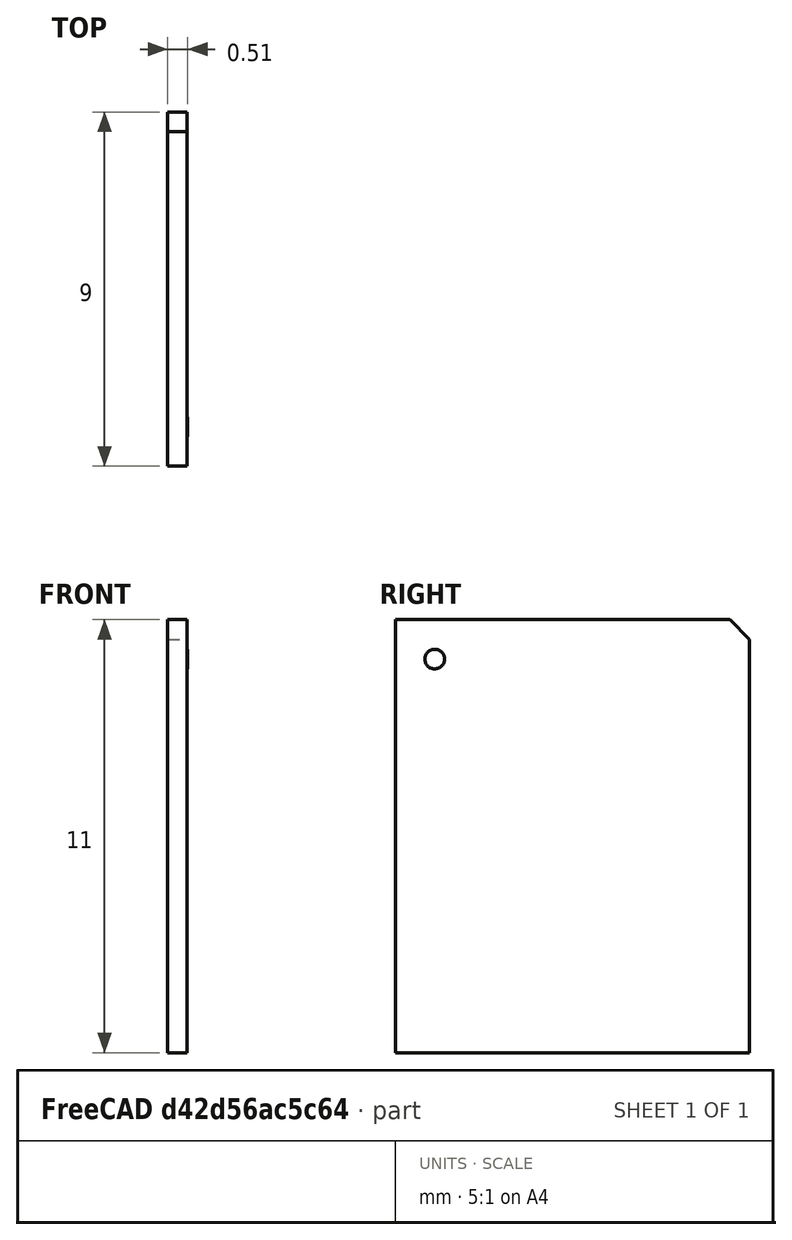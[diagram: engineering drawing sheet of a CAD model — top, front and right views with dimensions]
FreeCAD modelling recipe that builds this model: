
FCSTD DOCUMENT  (FreeCAD 1.1R20260108 (Git shallow))
Label: LiNbO3_Substrate_10mm
License: All rights reserved
LicenseURL: https://en.wikipedia.org/wiki/All_rights_reserved
objects: TechDraw::DrawViewAnnotation×5, TechDraw::DrawViewDimension×4, Sketcher::SketchObject×2, PartDesign::Pad×2, TechDraw::DrawProjGroupItem×2, App::Point×1, TechDraw::DrawSVGTemplate×1, PartDesign::Body×1, TechDraw::DrawProjGroup×1, TechDraw::DrawPage×1
note: 19 computed .brp shape members not serialized (recipe doc carries the construction recipe); baked Part::Feature solids carry a one-line shape summary decoded from their .brp

FEATURE [App::Point] Origin001
  Role = Origin
FEATURE [Sketcher::SketchObject] Sketch
  ArcFitTolerance = 1e-06
  AttachmentSupport = -> [Origin]
  ExternalTypes = [0]
  FullyConstrained = true
  MakeInternals = false
  MapMode = 5
  Placement = pos=(0,0,0) rot=(0.57735,0.57735,0.57735;2.0944rad)
  sketch-geometry (9):
    g0: LineSegment [constr] StartX=-4.5 StartY=-5.5 StartZ=0 EndX=4.5 EndY=-5.5 EndZ=0
    g1: LineSegment [constr] StartX=4.5 StartY=-5.5 StartZ=0 EndX=4.5 EndY=5.5 EndZ=0
    g2: LineSegment [constr] StartX=4.5 StartY=5.5 StartZ=0 EndX=-4.5 EndY=5.5 EndZ=0
    g3: LineSegment [constr] StartX=-4.5 StartY=5.5 StartZ=0 EndX=-4.5 EndY=-5.5 EndZ=0
    g4: LineSegment StartX=-4.5 StartY=-5.5 StartZ=0 EndX=4.5 EndY=-5.5 EndZ=0
    g5: LineSegment StartX=4.5 StartY=-5.5 StartZ=0 EndX=4.5 EndY=5 EndZ=0
    g6: LineSegment StartX=4 StartY=5.5 StartZ=0 EndX=4.5 EndY=5 EndZ=0
    g7: LineSegment StartX=4 StartY=5.5 StartZ=0 EndX=-4.5 EndY=5.5 EndZ=0
    g8: LineSegment StartX=-4.5 StartY=5.5 StartZ=0 EndX=-4.5 EndY=-5.5 EndZ=0
  constraints (24):
    c: Coincident(g0,g1)
    c: Coincident(g1,g2)
    c: Coincident(g2,g3)
    c: Coincident(g3,g0)
    c: Horizontal(g0)
    c: Horizontal(g2)
    c: Vertical(g1)
    c: Vertical(g3)
    c: Distance(g2,g2) = 9
    c: DistanceX(g-2,g2) = -4.5
    c: DistanceY(g-1,g0) = -5.5
    c: Coincident(g4,g0)
    c: Coincident(g4,g0)
    c: Coincident(g5,g0)
    c: PointOnObject(g5,g1)
    c: PointOnObject(g6,g2)
    c: Coincident(g6,g5)
    c: Distance(g5,g1) = 0.5
    c: Distance(g1,g6) = 0.5
    c: Coincident(g7,g6)
    c: Coincident(g7,g2)
    c: Coincident(g8,g2)
    c: Coincident(g8,g0)
    c: DistanceY(g8,g8) = 11
FEATURE [PartDesign::Pad] Pad
  Direction = (1,0,0)
  Length = 0.5
  Length2 = 10
  Profile = -> Sketch
  ReferenceAxis = -> Sketch [N_Axis]
  Refine = true
  SideType = 0
  Suppressed = false
  Type = 0
  Type2 = 0
FEATURE [TechDraw::DrawSVGTemplate] Template
  Height = 210
  Orientation = 1
  Template = /Applications/FreeCAD.app/Contents/Resources/share/Mod/TechDraw/Templates/ISO/A4_Landscape_TD.svg
  Width = 297
FEATURE [Sketcher::SketchObject] Sketch001
  ArcFitTolerance = 1e-06
  AttachmentSupport = -> [Pad]
  ExternalGeometry = -> [Pad]
  ExternalTypes = [0,0]
  FullyConstrained = true
  MakeInternals = false
  MapMode = 5
  Placement = pos=(0.5,0,0) rot=(0.57735,0.57735,0.57735;2.0944rad)
  sketch-geometry (1):
    g0: Circle CenterX=-3.5 CenterY=4.5 CenterZ=0 NormalX=0 NormalY=0 NormalZ=1 AngleXU=0 Radius=0.25
  constraints (3):
    c: DistanceY(g0,g-4) = 1
    c: DistanceX(g-4,g0) = 1
    c: Diameter(g0) = 0.5
FEATURE [PartDesign::Pad] Pad001
  BaseFeature = -> Pad
  Direction = (1,0,0)
  Length = 0.01
  Length2 = 10
  Profile = -> Sketch001
  ReferenceAxis = -> Sketch001 [N_Axis]
  Refine = true
  SideType = 0
  Suppressed = false
  Type = 0
  Type2 = 0
FEATURE [PartDesign::Body] Body
  AllowCompound = false
  Group = -> [Sketch,Pad,Sketch001,Pad001]
  Origin = -> Origin
  Tip = -> Pad001
FEATURE [TechDraw::DrawProjGroupItem] ProjItem  label="Front"
  CoarseView = false
  Direction = (1,0,0)
  Focus = 100
  HardHidden = true
  IsoCount = 0
  IsoHidden = false
  IsoVisible = false
  LockPosition = true
  Perspective = false
  Rotation = 0
  RotationVector = (0,1,0)
  Scale = 5
  ScaleType = 2
  ScrubCount = 1
  SeamHidden = false
  SeamVisible = false
  SmoothHidden = false
  SmoothVisible = true
  Source = -> [Body]
  Type = 0
  X = 0
  XDirection = (0,1,0)
  Y = 0
FEATURE [TechDraw::DrawProjGroupItem] ProjItem001  label="FrontTopRight"
  CoarseView = false
  Direction = (0.57735,0.57735,0.57735)
  Focus = 100
  HardHidden = true
  IsoCount = 0
  IsoHidden = false
  IsoVisible = false
  LockPosition = false
  Perspective = false
  Rotation = 0
  RotationVector = (1,0,0)
  Scale = 5
  ScaleType = 2
  ScrubCount = 1
  SeamHidden = false
  SeamVisible = false
  SmoothHidden = false
  SmoothVisible = true
  Source = -> [Body]
  Type = 7
  X = -54.2938
  XDirection = (-0.707107,0.707107,0)
  Y = -74.6496
FEATURE [TechDraw::DrawProjGroup] ProjGroup
  Anchor = -> ProjItem
  AutoDistribute = true
  LockPosition = false
  ProjectionType = 0
  Rotation = 0
  Scale = 5
  ScaleType = 2
  Source = -> [Body]
  Views = -> [ProjItem,ProjItem001]
  X = 147.964
  Y = 136.218
  spacingX = 15
  spacingY = 15
FEATURE [TechDraw::DrawViewAnnotation] Annotation
  Font = osifont
  LineSpace = 100
  LockPosition = false
  MaxWidth = -1
  Rotation = 0
  ScaleType = 0
  Text = +Z
  TextSize = 5
  TextStyle = 0
  X = 93.6698
  Y = 110.213
FEATURE [TechDraw::DrawViewAnnotation] Annotation001
  Font = osifont
  LineSpace = 100
  LockPosition = false
  MaxWidth = -1
  Rotation = 0
  ScaleType = 0
  Text = +Y
  TextSize = 5
  TextStyle = 0
  X = 128.644
  Y = 42.1354
FEATURE [TechDraw::DrawViewAnnotation] Annotation002
  Font = osifont
  LineSpace = 100
  LockPosition = false
  MaxWidth = -1
  Rotation = 0
  ScaleType = 0
  Text = +X
  TextSize = 5
  TextStyle = 0
  X = 50.7535
  Y = 43.6687
FEATURE [TechDraw::DrawViewDimension] Dimension
  AngleOverride = false
  Arbitrary = false
  ArbitraryTolerances = false
  BoxCorners = (2) [(-22.5,-27.5,0),(22.5,27.5,0)]
  EqualTolerance = true
  ExtensionAngle = 0
  FormatSpec = %.2w
  FormatSpecOverTolerance = %+.2w
  FormatSpecUnderTolerance = %+.2w
  Inverted = false
  LineAngle = 0
  LockPosition = false
  MeasureType = 1
  OverTolerance = 0.2
  References2D = -> [ProjItem]
  Rotation = 0
  ScaleType = 0
  ShowUnits = false
  TheoreticalExact = false
  Type = 1
  UnderTolerance = -0.2
  UseActualArea = true
  X = 0
  Y = -32.9551
FEATURE [TechDraw::DrawViewDimension] Dimension001
  AngleOverride = false
  Arbitrary = false
  ArbitraryTolerances = false
  BoxCorners = (2) [(-22.5,-27.5,0),(22.5,27.5,0)]
  EqualTolerance = true
  ExtensionAngle = 0
  FormatSpec = %.2w
  FormatSpecOverTolerance = %+.2w
  FormatSpecUnderTolerance = %+.2w
  Inverted = false
  LineAngle = 0
  LockPosition = false
  MeasureType = 1
  OverTolerance = 0.2
  References2D = -> [ProjItem]
  Rotation = 0
  ScaleType = 0
  ShowUnits = false
  TheoreticalExact = false
  Type = 2
  UnderTolerance = -0.2
  UseActualArea = true
  X = -34.1514
  Y = 0
FEATURE [TechDraw::DrawViewDimension] Dimension002
  AngleOverride = false
  Arbitrary = true
  ArbitraryTolerances = false
  BoxCorners = (2) [(-22.5,-27.5,0),(22.5,27.5,0)]
  EqualTolerance = true
  ExtensionAngle = 0
  FormatSpec = approx. 1.0
  FormatSpecOverTolerance = %+.2w
  FormatSpecUnderTolerance = %+.2w
  Inverted = false
  LineAngle = 0
  LockPosition = false
  MeasureType = 1
  OverTolerance = 0
  References2D = -> [ProjItem]
  Rotation = 0
  ScaleType = 0
  ShowUnits = false
  TheoreticalExact = false
  Type = 1
  UnderTolerance = 0
  UseActualArea = true
  X = -42.4072
  Y = 38.9928
FEATURE [TechDraw::DrawViewDimension] Dimension003
  AngleOverride = false
  Arbitrary = true
  ArbitraryTolerances = false
  BoxCorners = (2) [(-22.5,-27.5,0),(22.5,27.5,0)]
  EqualTolerance = true
  ExtensionAngle = 0
  FormatSpec = approx. 0.5
  FormatSpecOverTolerance = %+.2w
  FormatSpecUnderTolerance = %+.2w
  Inverted = false
  LineAngle = 0
  LockPosition = false
  MeasureType = 1
  OverTolerance = 0
  References2D = -> [ProjItem]
  Rotation = 0
  ScaleType = 0
  ShowUnits = false
  TheoreticalExact = false
  Type = 1
  UnderTolerance = 0
  UseActualArea = true
  X = 43.4555
  Y = 38.9928
FEATURE [TechDraw::DrawViewAnnotation] Annotation003
  Font = osifont
  LineSpace = 100
  LockPosition = false
  MaxWidth = -1
  Rotation = 0
  ScaleType = 0
  Text = dye mark on +X face
  TextSize = 5
  TextStyle = 0
  X = 89.3922
  Y = 187.184
FEATURE [TechDraw::DrawViewAnnotation] Annotation004
  Font = osifont
  LineSpace = 100
  LockPosition = false
  MaxWidth = -1
  Rotation = 0
  ScaleType = 0
  Text = visible chamfer
  TextSize = 5
  TextStyle = 0
  X = 197.335
  Y = 187.184
FEATURE [TechDraw::DrawPage] Page
  KeepUpdated = true
  NextBalloonIndex = 1
  ProjectionType = 0
  Template = -> Template
  Views = -> [ProjGroup,Annotation,Annotation001,Annotation002,Dimension,Dimension001,Dimension002,Dimension003,Annotation003,Annotation004]
